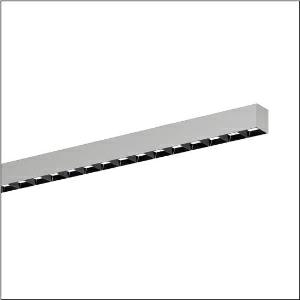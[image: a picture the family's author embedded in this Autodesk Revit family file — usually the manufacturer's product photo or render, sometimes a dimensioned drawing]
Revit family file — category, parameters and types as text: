
# Revit family: silica_r__21_51mx24tctas_d744
name_source: partatom
category: Lighting Fixtures
units: mm (PartAtom-declared; Revit-internal decimal feet)

## family parameters
Cut with Voids When Loaded = No
Host = Face
Light Source = No
Part Type = Normal
Room Calculation Point = No
Round Connector Dimension = Use Diameter
Shared = No

## types (1)
- --- (1 x LED, 8200 lm, 81.1 W, 6500K)
    Apparent Load = 81 VA
    CIE Flux Codes = 74 94 99 100 100
    Color Rendering = 80
    Color Temperature = 6500K
    Default Elevation = 1800 mm
    Description = Silica® 21, office luminaire, primary light control with darklight reflector, of PMMA, black, light emission: direct distribution, primary light characteristic: asymmetric, installation type: surface-mounted, LED, rated luminous flux: 8.200lm, luminous efficacy: 96lm/W, light colour: 8tw, colour temperature: 2700..6500K, control gear: ECG DALI, with terminal, 3+2-pole, max. 2.5mm², mains connection: 220..240V, AC, 50/60Hz, rated input power: 85.2W, luminaire housing, of aluminium, metallic grey (RAL 9006), length: 3.004mm, width: 53mm, height: 53mm, protection rating (complete): IP20, insulation class (complete): insulation class I (protective earthing), certification: CE, permissible operating ambient temperature: 0..+35°C, standard: EN 50419, packaging unit: 1 piece
    Height = 0 mm  [stored 0 ft]
    Lamp = 1 x LED
    Lamp Light Flux = 8200 lm
    Lamp Power = 81.1 W
    Lamp count = 1
    Length = 3004 mm
    Luminous efficacy = 101 lm/W
    Manufacturer = Siteco
    ModVariant = No
    Model = 51MX24TCTAS
    Mounting Place = Ceiling
    Mounting Type = Recessed
    Number of Poles = 1
    OnlyDefault = Yes
    Power Factor = 1
    Product Name = Silica® 21
    Product group = office luminaire | ceiling recessed
    ProductGroupID = 401
    Protection Class = Protection class I
    Protection Degree = IP 20
    RLX_Detail_Level = 1
    RLX_Emergency_Light_Flux = 0 lm
    RLX_Emergency_Type = 0
    RLX_Emergency_Type_DB = No
    RlxData = <blob elided: 60193 chars, md5=973a2c35>
    Socket = socket
    Standby Power = 0 W
    System Light Flux = 8200 lm
    System Power = 81 W
    Type Comments = individual setting
    Type Image = l_1313585.jpg
    URL = http://relux.com
    VarID = @adj_089337
    Voltage = 0 V
    Weight = 0.00 kg
    Width = 53 mm

note: [stored X ft] marks values corroborated as IEEE doubles in the binary element streams (Revit-internal decimal feet)

## geometry (parser evidence)
native form markers: Blend x4, Sweep x12
no freeform markers — native parametric forms only
